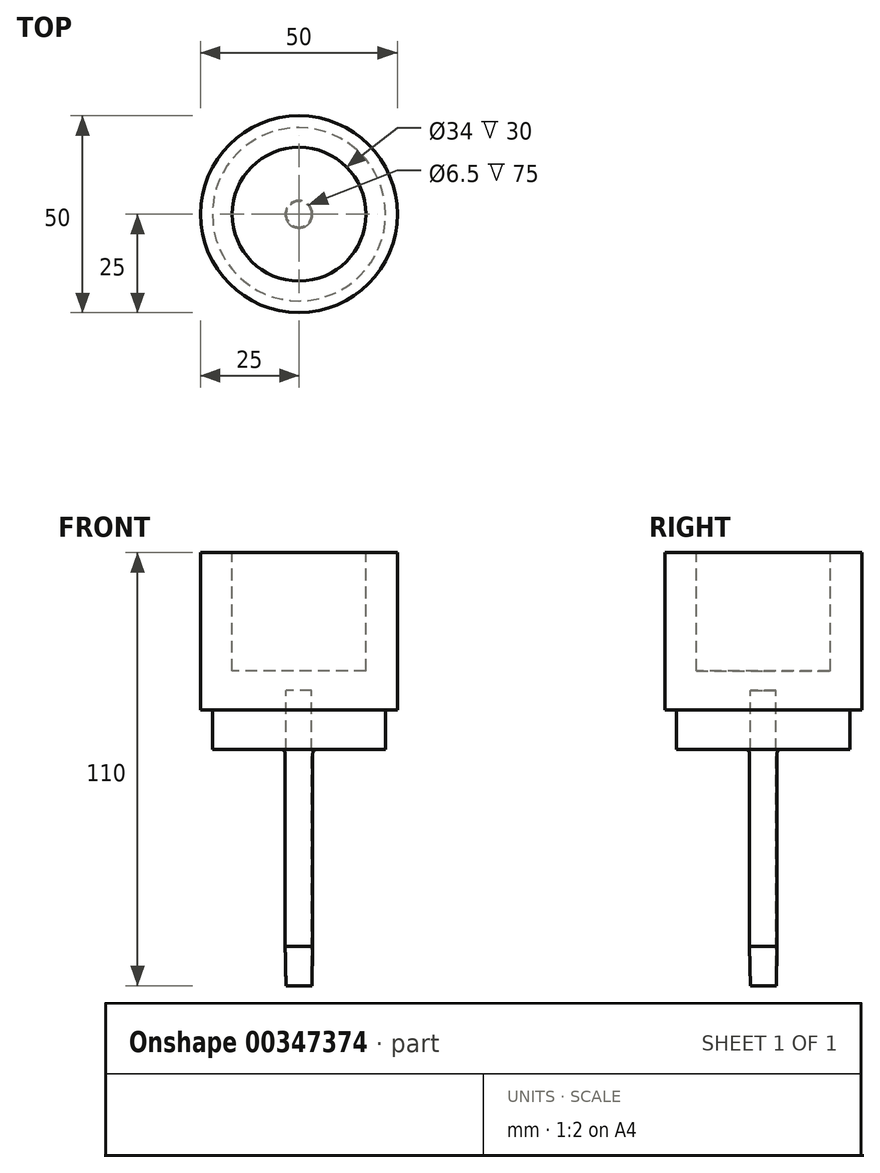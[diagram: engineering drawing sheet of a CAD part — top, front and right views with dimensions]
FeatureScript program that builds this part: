
annotation { "Feature Type Name" : "Feature", "Feature Type Description" : "" }
export const myFeature = defineFeature(function(context is Context, id is Id, definition is map)
    precondition{}
    {
        {
            var Q0;
            Q0=qCreatedBy(makeId("Front.planeOp"),FACE);
            var sketch = newSketch(context, id + "F0", { "sketchPlane" : qUnion([Q0])});
            skLineSegment(sketch, "E0", {"start": v(0, 74.18) * mm, "end": v(0, -71.18) * mm});
            skLineSegment(sketch, "E1.0", {"start": v(-3.5, 28.18) * mm, "end": v(-3.5, -30.82) * mm});
            skLineSegment(sketch, "E2.0", {"start": v(-25, 79.18) * mm, "end": v(-25, 39.18) * mm});
            skLineSegment(sketch, "E3.0", {"start": v(-3.25, 44.18) * mm, "end": v(-3.25, -30.82) * mm});
            skLineSegment(sketch, "E4.0", {"start": v(-22, 29.18) * mm, "end": v(-4.5, 29.18) * mm});
            skLineSegment(sketch, "E5.0", {"start": v(-3.25, 44.18) * mm, "end": v(0, 44.18) * mm});
            skLineSegment(sketch, "E6.0", {"start": v(-17, 79.18) * mm, "end": v(-17, 49.18) * mm});
            skLineSegment(sketch, "E7.0", {"start": v(-3.5, -30.82) * mm, "end": v(-3.25, -30.82) * mm});
            skLineSegment(sketch, "E8.0", {"start": v(-17, 49.18) * mm, "end": v(0, 49.18) * mm});
            skLineSegment(sketch, "E9.0", {"start": v(-25, 79.18) * mm, "end": v(-17, 79.18) * mm});
            skPoint(sketch, "E10.visualSharp", {"position": v(-3.5, 29.18) * mm});
            skArc(sketch, "E10.filletArc", {"start": v(-3.5, 28.18) * mm, "mid": v(-3.8, 28.89) * mm, "end": v(-4.5, 29.18) * mm});
            skLineSegment(sketch, "E11.0", {"start": v(-22, 39.18) * mm, "end": v(-22, 29.18) * mm});
            skLineSegment(sketch, "E12.0", {"start": v(-25, 39.18) * mm, "end": v(-22, 39.18) * mm});
            skSolve(sketch);
        }
        {
            var Q0;
            Q0=makeQuery(id+"F0.imprint","IMPRINT",FACE,{"disambiguationData":[TD([[makeQuery(id+"F0.imprint","IMPRINT",EDGE,{"derivedFrom":sQuery(id+"F0.wireOp",EDGE,"E1.0")}),1.0]])]});
            var Q1;
            Q1=sQuery(id+"F0.wireOp",EDGE,"E0");
            revolve(context, id + "F1", {"surfaceOperationType" : NewSurfaceOperationType.NEW, "entities" : qUnion([Q0]), "axis" : qUnion([Q1]), "revolveType" : RevolveType.FULL});
        }
        {
            var Q0;
            Q0=makeQuery(id+"F1.opRevolve","SWEPT_EDGE",EDGE,{"disambiguationData":[OSD([sQuery(id+"F0.wireOp",EDGE,"E1.0"),sQuery(id+"F0.wireOp",EDGE,"E7.0")])]});
            chamfer(context, id + "F2", {"entities" : qUnion([Q0]), "chamferType" : ChamferType.TWO_OFFSETS, "width1" : 10 * mm, "oppositeDirection" : false, "width2" : 0.2 * mm, "tangentPropagation" : true});
        }
    });
